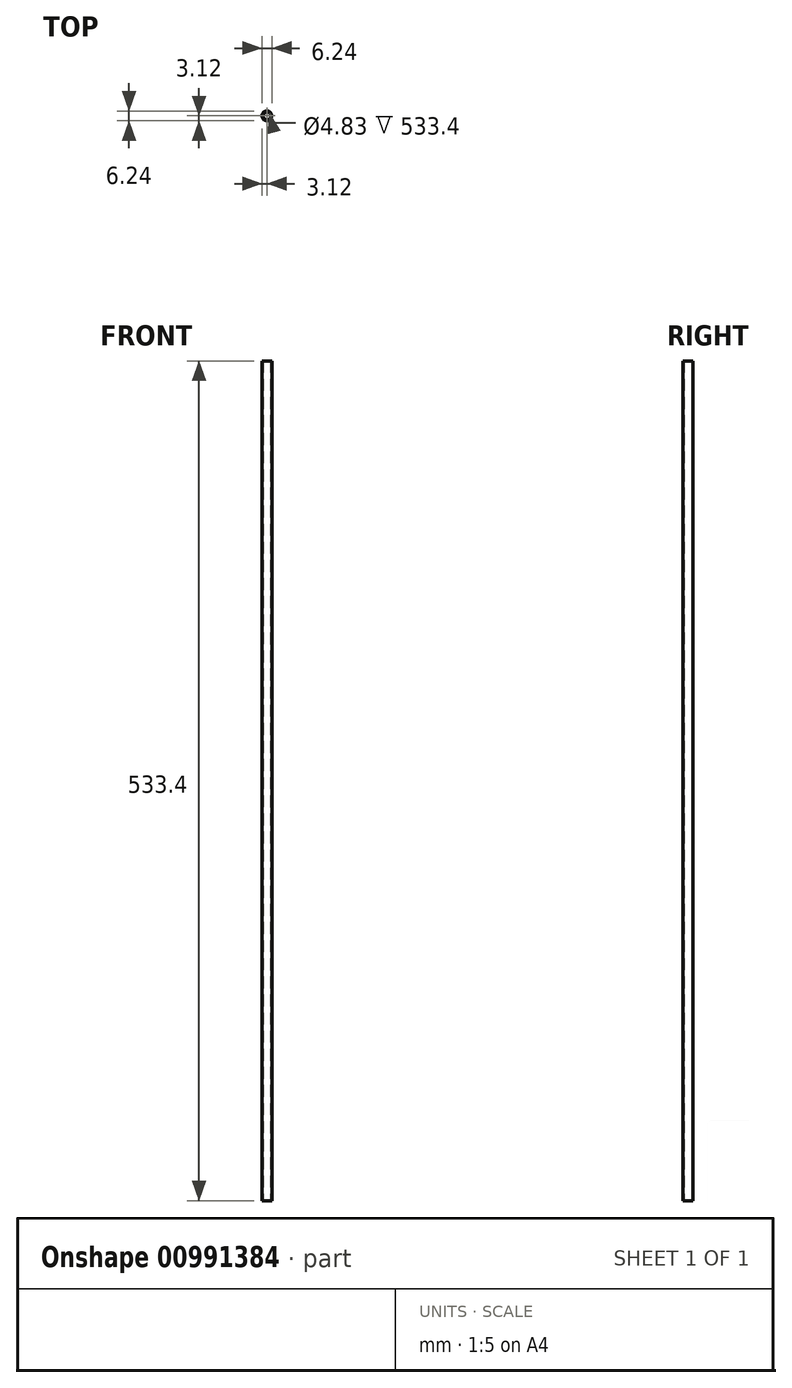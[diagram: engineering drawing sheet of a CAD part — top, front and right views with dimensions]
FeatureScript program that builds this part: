
annotation { "Feature Type Name" : "Feature", "Feature Type Description" : "" }
export const myFeature = defineFeature(function(context is Context, id is Id, definition is map)
    precondition{}
    {
        {
            var Q0;
            Q0=qCreatedBy(makeId("Top.planeOp"),FACE);
            var sketch = newSketch(context, id + "F0", { "sketchPlane" : qUnion([Q0])});
            skCircle(sketch, "E0", {"center": v(0, 0) * mm, "radius": 3.12 * mm});
            skCircle(sketch, "E1", {"center": v(0, 0) * mm, "radius": 2.41 * mm});
            skSolve(sketch);
        }
        {
            var Q0;
            Q0 = qSketchRegion(id + "F0", true);
            extrude(context, id + "F1", {"entities" : qUnion([Q0]), "endBound" : BoundingType.SYMMETRIC, "depth" : 533.4 * mm, "offsetDistance" : 25.4 * mm});
        }
    });
